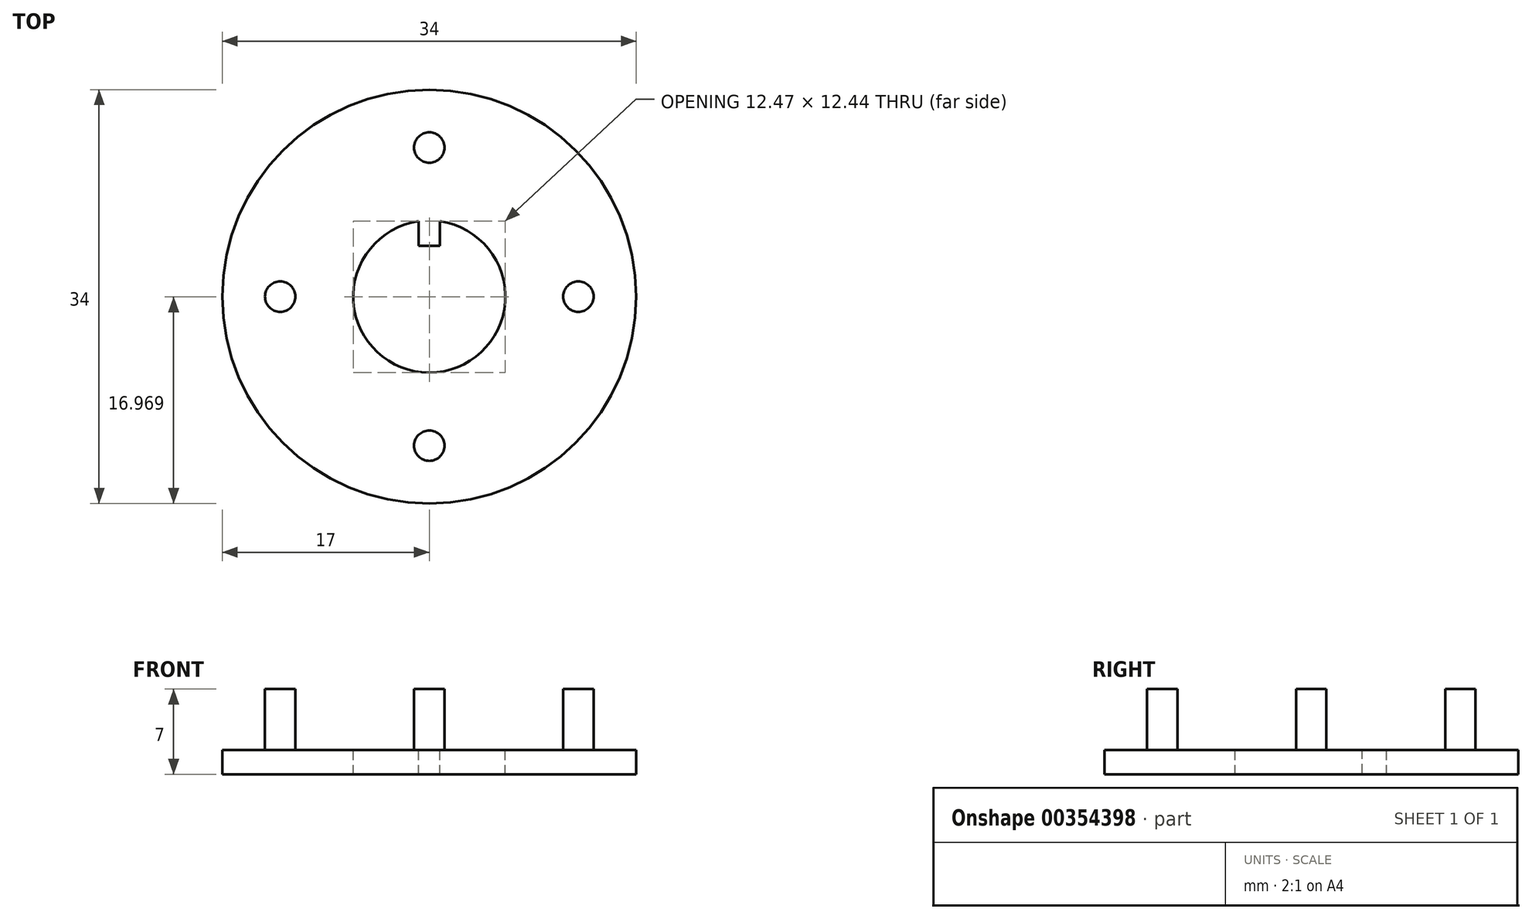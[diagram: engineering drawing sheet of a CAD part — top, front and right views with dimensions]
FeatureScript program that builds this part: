
annotation { "Feature Type Name" : "Feature", "Feature Type Description" : "" }
export const myFeature = defineFeature(function(context is Context, id is Id, definition is map)
    precondition{}
    {
        {
            assignVariable(context, id + "F0", {"name" : "post_height", "anyValue" : 5});
        }
        {
            assignVariable(context, id + "F1", {"name" : "plate_thickness", "anyValue" : 2});
        }
        {
            var Q0;
            Q0=qCreatedBy(makeId("Top.planeOp"),FACE);
            var sketch = newSketch(context, id + "F2", { "sketchPlane" : qUnion([Q0])});
            skLineSegment(sketch, "E0.bottom", {"start": v(13.5, 1.25) * mm, "end": v(-13.5, 1.25) * mm});
            skLineSegment(sketch, "E0.top", {"start": v(13.5, -1.25) * mm, "end": v(-13.5, -1.25) * mm});
            skLineSegment(sketch, "E0.left", {"start": v(13.5, 1.25) * mm, "end": v(13.5, -1.25) * mm});
            skLineSegment(sketch, "E0.right", {"start": v(-13.5, 1.25) * mm, "end": v(-13.5, -1.25) * mm});
            skPoint(sketch, "E0.middle", {"position": v(0, 0) * mm});
            skSolve(sketch);
        }
        {
            var Q0;
            Q0=makeQuery(id+"F2.imprint","IMPRINT",FACE,{"disambiguationData":[TD([[makeQuery(id+"F2.imprint","IMPRINT",EDGE,{"derivedFrom":sQuery(id+"F2.wireOp",EDGE,"E0.bottom")}),1.0]])]});
            extrude(context, id + "F3", {"entities" : qUnion([Q0]), "depth" : (getVariable(context, 'plate_thickness')) * mm});
        }
        {
            var Q0;
            Q0=qCreatedBy(makeId("Top.planeOp"),FACE);
            var sketch = newSketch(context, id + "F4", { "sketchPlane" : qUnion([Q0])});
            skLineSegment(sketch, "E1.bottom", {"start": v(1.25, 13.5) * mm, "end": v(-1.25, 13.5) * mm});
            skLineSegment(sketch, "E1.top", {"start": v(1.25, -13.5) * mm, "end": v(-1.25, -13.5) * mm});
            skLineSegment(sketch, "E1.left", {"start": v(1.25, 13.5) * mm, "end": v(1.25, -13.5) * mm});
            skLineSegment(sketch, "E1.right", {"start": v(-1.25, 13.5) * mm, "end": v(-1.25, -13.5) * mm});
            skPoint(sketch, "E1.middle", {"position": v(0, 0) * mm});
            skSolve(sketch);
        }
        {
            var Q0;
            Q0 = qSketchRegion(id + "F4", true);
            extrude(context, id + "F5", {"entities" : qUnion([Q0]), "operationType" : NewBodyOperationType.ADD, "depth" : (getVariable(context, 'plate_thickness')) * mm});
        }
        {
            var Q0;
            Q0=makeQuery(id+"F5.boolean.opBoolean","MERGE",FACE,{"derivedFrom":[makeQuery(id+"F3.opExtrude","CAP_FACE",FACE,{"disambiguationData":[OSD([sQuery(id+"F2.wireOp",EDGE,"E0.bottom"),sQuery(id+"F2.wireOp",EDGE,"E0.top"),sQuery(id+"F2.wireOp",EDGE,"E0.left"),sQuery(id+"F2.wireOp",EDGE,"E0.right")])],"isStart":false}),makeQuery(id+"F5.opExtrude","CAP_FACE",FACE,{"disambiguationData":[OSD([sQuery(id+"F4.wireOp",EDGE,"E1.bottom"),sQuery(id+"F4.wireOp",EDGE,"E1.top"),sQuery(id+"F4.wireOp",EDGE,"E1.left"),sQuery(id+"F4.wireOp",EDGE,"E1.right")])],"isStart":false})]});
            var sketch = newSketch(context, id + "F6", { "sketchPlane" : qUnion([Q0])});
            skLineSegment(sketch, "E2", {"start": v(0, 13.5) * mm, "end": v(0, 12.25) * mm, "construction": true});
            skPoint(sketch, "E2.endSnap0", {"position": v(0, 13.5) * mm});
            skLineSegment(sketch, "E3", {"start": v(0, -13.5) * mm, "end": v(0, -12.25) * mm, "construction": true});
            skPoint(sketch, "E3.endSnap0", {"position": v(0, -13.5) * mm});
            skLineSegment(sketch, "E4", {"start": v(-13.5, 0) * mm, "end": v(-12.25, 0) * mm, "construction": true});
            skPoint(sketch, "E4.endSnap0", {"position": v(-13.5, 0) * mm});
            skLineSegment(sketch, "E5", {"start": v(13.5, 0) * mm, "end": v(12.25, 0) * mm, "construction": true});
            skCircle(sketch, "E6", {"center": v(-12.25, 0) * mm, "radius": 1.25 * mm});
            skCircle(sketch, "E7", {"center": v(12.25, 0) * mm, "radius": 1.25 * mm});
            skCircle(sketch, "E8", {"center": v(0, 12.25) * mm, "radius": 1.25 * mm});
            skCircle(sketch, "E9", {"center": v(0, -12.25) * mm, "radius": 1.25 * mm});
            skSolve(sketch);
        }
        {
            var Q0;
            {var subQ0=sQuery(id+"F6.wireOp",EDGE,"E6");var subQ1=sQuery(id+"F2.wireOp",EDGE,"E0.right");var subQ2=makeQuery(id+"F6.imprint","INTERSECT",VERTEX,{"derivedFrom":[makeQuery(id+"F3.opExtrude","CAP_EDGE",EDGE,{"disambiguationData":[OSD([subQ1])],"isStart":false}),subQ0]});Q0=makeQuery(id+"F6.imprint","IMPRINT",FACE,{"disambiguationData":[TD([[makeQuery(id+"F6.imprint","IMPRINT",EDGE,{"disambiguationData":[TD([[subQ2,1.0]])],"derivedFrom":subQ0}),1.0]])]});}
            var Q1;
            {var subQ0=sQuery(id+"F6.wireOp",EDGE,"E8");var subQ1=sQuery(id+"F4.wireOp",EDGE,"E1.bottom");var subQ2=makeQuery(id+"F6.imprint","INTERSECT",VERTEX,{"derivedFrom":[makeQuery(id+"F5.opExtrude","CAP_EDGE",EDGE,{"disambiguationData":[OSD([subQ1])],"isStart":false}),subQ0]});Q1=makeQuery(id+"F6.imprint","IMPRINT",FACE,{"disambiguationData":[TD([[makeQuery(id+"F6.imprint","IMPRINT",EDGE,{"disambiguationData":[TD([[subQ2,1.0]])],"derivedFrom":subQ0}),1.0]])]});}
            var Q2;
            {var subQ0=sQuery(id+"F6.wireOp",EDGE,"E7");var subQ1=sQuery(id+"F2.wireOp",EDGE,"E0.left");var subQ10=makeQuery(id+"F6.imprint","INTERSECT",VERTEX,{"derivedFrom":[makeQuery(id+"F3.opExtrude","CAP_EDGE",EDGE,{"disambiguationData":[OSD([subQ1])],"isStart":false}),subQ0]});Q2=makeQuery(id+"F6.imprint","IMPRINT",FACE,{"disambiguationData":[TD([[makeQuery(id+"F6.imprint","IMPRINT",EDGE,{"disambiguationData":[TD([[subQ10,-1.0]])],"derivedFrom":subQ0}),1.0]])]});}
            var Q3;
            {var subQ0=sQuery(id+"F6.wireOp",EDGE,"E9");var subQ1=sQuery(id+"F4.wireOp",EDGE,"E1.top");var subQ11=makeQuery(id+"F6.imprint","INTERSECT",VERTEX,{"derivedFrom":[makeQuery(id+"F5.opExtrude","CAP_EDGE",EDGE,{"disambiguationData":[OSD([subQ1])],"isStart":false}),subQ0]});Q3=makeQuery(id+"F6.imprint","IMPRINT",FACE,{"disambiguationData":[TD([[makeQuery(id+"F6.imprint","IMPRINT",EDGE,{"disambiguationData":[TD([[subQ11,1.0]])],"derivedFrom":subQ0}),1.0]])]});}
            extrude(context, id + "F7", {"entities" : qUnion([Q0, Q1, Q2, Q3]), "operationType" : NewBodyOperationType.ADD, "depth" : (getVariable(context, 'post_height')) * mm});
        }
        {
            var Q0;
            Q0=qCreatedBy(makeId("Top.planeOp"),FACE);
            var sketch = newSketch(context, id + "F8", { "sketchPlane" : qUnion([Q0])});
            skCircle(sketch, "E10", {"center": v(0, 0) * mm, "radius": 17 * mm});
            skSolve(sketch);
        }
        {
            var Q0;
            Q0 = qSketchRegion(id + "F8", true);
            extrude(context, id + "F9", {"entities" : qUnion([Q0]), "operationType" : NewBodyOperationType.ADD, "depth" : (getVariable(context, 'plate_thickness')) * mm});
        }
        {
            var Q0;
            {var subQ0=sQuery(id+"F2.wireOp",EDGE,"E0.top");var subQ1=makeQuery(id+"F3.opExtrude","SWEPT_FACE",FACE,{"disambiguationData":[OSD([subQ0])]});var subQ2=sQuery(id+"F4.wireOp",EDGE,"E1.right");var subQ3=sQuery(id+"F4.wireOp",EDGE,"E1.left");var subQ4=sQuery(id+"F4.wireOp",EDGE,"E1.top");var subQ5=sQuery(id+"F4.wireOp",EDGE,"E1.bottom");var subQ6=makeQuery(id+"F5.opExtrude","CAP_FACE",FACE,{"disambiguationData":[OSD([subQ5,subQ4,subQ3,subQ2])],"isStart":false});var subQ7=sQuery(id+"F2.wireOp",EDGE,"E0.right");var subQ8=sQuery(id+"F2.wireOp",EDGE,"E0.left");var subQ9=sQuery(id+"F2.wireOp",EDGE,"E0.bottom");var subQ10=makeQuery(id+"F3.opExtrude","CAP_FACE",FACE,{"disambiguationData":[OSD([subQ9,subQ0,subQ8,subQ7])],"isStart":false});var subQ11=makeQuery(id+"F3.opExtrude","SWEPT_FACE",FACE,{"disambiguationData":[OSD([subQ9])]});var subQ12=makeQuery(id+"F5.opExtrude","SWEPT_FACE",FACE,{"disambiguationData":[OSD([subQ3])]});var subQ13=makeQuery(id+"F5.opExtrude","SWEPT_FACE",FACE,{"disambiguationData":[OSD([subQ2])]});var subQ14=makeQuery(id+"F7.opExtrude","SWEPT_FACE",FACE,{"disambiguationData":[OSD([sQuery(id+"F6.wireOp",EDGE,"E6")])]});var subQ15=makeQuery(id+"F7.opExtrude","SWEPT_FACE",FACE,{"disambiguationData":[OSD([sQuery(id+"F6.wireOp",EDGE,"E7")])]});var subQ16=makeQuery(id+"F7.opExtrude","SWEPT_FACE",FACE,{"disambiguationData":[OSD([sQuery(id+"F6.wireOp",EDGE,"E8")])]});var subQ17=makeQuery(id+"F7.opExtrude","SWEPT_FACE",FACE,{"disambiguationData":[OSD([sQuery(id+"F6.wireOp",EDGE,"E9")])]});var subQ18=makeQuery(id+"F5.boolean.opBoolean","MERGE",FACE,{"derivedFrom":[subQ10,subQ6]});var subQ19=makeQuery(id+"F5.opExtrude","SWEPT_FACE",FACE,{"disambiguationData":[OSD([subQ4])]});var subQ20=makeQuery(id+"F5.opExtrude","SWEPT_FACE",FACE,{"disambiguationData":[OSD([subQ5])]});var subQ21=makeQuery(id+"F3.opExtrude","SWEPT_FACE",FACE,{"disambiguationData":[OSD([subQ7])]});var subQ22=makeQuery(id+"F3.opExtrude","SWEPT_FACE",FACE,{"disambiguationData":[OSD([subQ8])]});Q0=makeQuery(id+"F9.boolean.opBoolean","MERGE",FACE,{"derivedFrom":[makeQuery(id+"F7.boolean.opBoolean","SPLIT",FACE,{"disambiguationData":[TD([subQ11,subQ10,subQ22,subQ6,subQ15])],"derivedFrom":subQ18}),makeQuery(id+"F7.boolean.opBoolean","SPLIT",FACE,{"disambiguationData":[TD([subQ10,subQ1,subQ22,subQ6,subQ15])],"derivedFrom":subQ18}),makeQuery(id+"F7.boolean.opBoolean","SPLIT",FACE,{"disambiguationData":[TD([subQ11,subQ10,subQ21,subQ6,subQ14])],"derivedFrom":subQ18}),makeQuery(id+"F7.boolean.opBoolean","SPLIT",FACE,{"disambiguationData":[TD([subQ10,subQ1,subQ21,subQ6,subQ14])],"derivedFrom":subQ18}),makeQuery(id+"F7.boolean.opBoolean","SPLIT",FACE,{"disambiguationData":[TD([subQ10,subQ20,subQ6,subQ12,subQ16])],"derivedFrom":subQ18}),makeQuery(id+"F7.boolean.opBoolean","SPLIT",FACE,{"disambiguationData":[TD([subQ10,subQ20,subQ6,subQ13,subQ16])],"derivedFrom":subQ18}),makeQuery(id+"F7.boolean.opBoolean","SPLIT",FACE,{"disambiguationData":[TD([subQ10,subQ6,subQ19,subQ12,subQ17])],"derivedFrom":subQ18}),makeQuery(id+"F7.boolean.opBoolean","SPLIT",FACE,{"disambiguationData":[TD([subQ10,subQ6,subQ19,subQ13,subQ17])],"derivedFrom":subQ18}),makeQuery(id+"F7.boolean.opBoolean","SPLIT",FACE,{"disambiguationData":[TD([subQ11,subQ10,subQ1,subQ6,subQ12,subQ13,subQ14,subQ15,subQ16,subQ17])],"derivedFrom":subQ18}),makeQuery(id+"F9.opExtrude","CAP_FACE",FACE,{"disambiguationData":[OSD([sQuery(id+"F8.wireOp",EDGE,"E10")])],"isStart":false})]});}
            var sketch = newSketch(context, id + "F10", { "sketchPlane" : qUnion([Q0])});
            skCircle(sketch, "E11", {"center": v(0, 0) * mm, "radius": 6.25 * mm});
            skSolve(sketch);
        }
        {
            var Q0;
            Q0=makeQuery(id+"F10.imprint","IMPRINT",FACE,{"disambiguationData":[TD([[makeQuery(id+"F10.imprint","IMPRINT",EDGE,{"derivedFrom":sQuery(id+"F10.wireOp",EDGE,"E11")}),1.0]])]});
            extrude(context, id + "F11", {"entities" : qUnion([Q0]), "operationType" : NewBodyOperationType.REMOVE, "endBound" : BoundingType.UP_TO_NEXT, "oppositeDirection" : true, "depth" : 25 * mm});
        }
        {
            var Q0;
            Q0=qCreatedBy(makeId("Top.planeOp"),FACE);
            var sketch = newSketch(context, id + "F12", { "sketchPlane" : qUnion([Q0])});
            skLineSegment(sketch, "E12", {"start": v(0, 0) * mm, "end": v(0, 6.25) * mm, "construction": true});
            skLineSegment(sketch, "E13.bottom", {"start": v(0.87, 4.17) * mm, "end": v(-0.88, 4.17) * mm});
            skLineSegment(sketch, "E13.top", {"start": v(0.88, 8.33) * mm, "end": v(-0.87, 8.33) * mm});
            skLineSegment(sketch, "E13.left", {"start": v(0.87, 4.17) * mm, "end": v(0.88, 8.33) * mm});
            skLineSegment(sketch, "E13.right", {"start": v(-0.88, 4.17) * mm, "end": v(-0.87, 8.33) * mm});
            skPoint(sketch, "E13.middle", {"position": v(0, 6.25) * mm});
            skSolve(sketch);
        }
        {
            var Q0;
            Q0=makeQuery(id+"F12.imprint","IMPRINT",FACE,{"disambiguationData":[TD([[makeQuery(id+"F12.imprint","IMPRINT",EDGE,{"derivedFrom":sQuery(id+"F12.wireOp",EDGE,"E13.bottom")}),-1.0]])]});
            extrude(context, id + "F13", {"entities" : qUnion([Q0]), "operationType" : NewBodyOperationType.ADD, "depth" : (getVariable(context, 'plate_thickness')) * mm});
        }
    });
